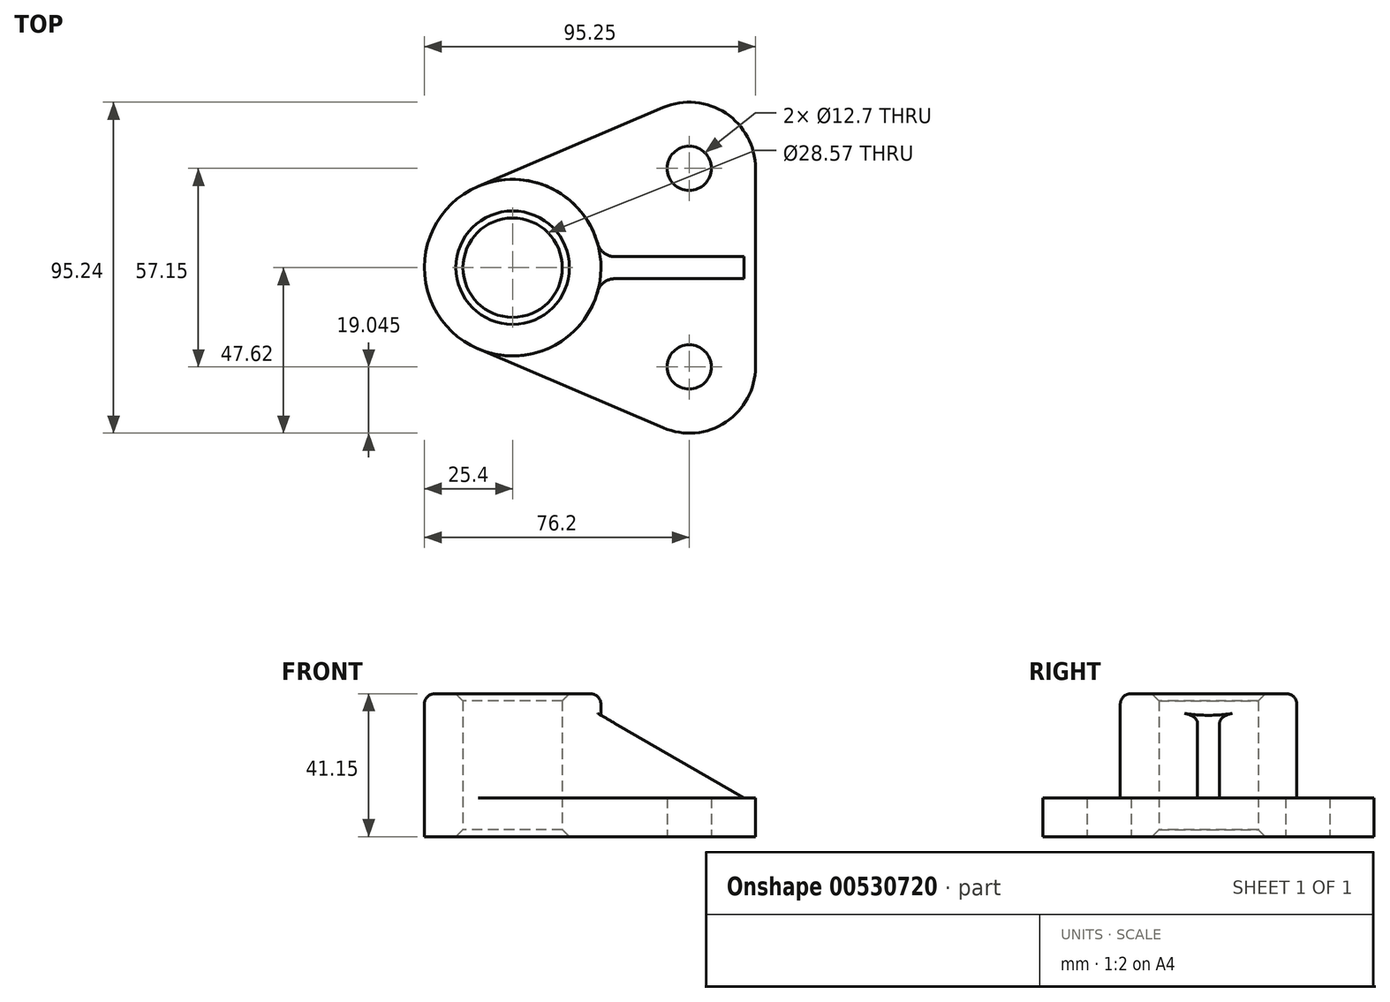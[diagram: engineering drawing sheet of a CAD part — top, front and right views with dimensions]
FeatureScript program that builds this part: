
annotation { "Feature Type Name" : "Feature", "Feature Type Description" : "" }
export const myFeature = defineFeature(function(context is Context, id is Id, definition is map)
    precondition{}
    {
        {
            var Q0;
            Q0=qCreatedBy(makeId("Top.planeOp"),FACE);
            var sketch = newSketch(context, id + "F0", { "sketchPlane" : qUnion([Q0])});
            skArc(sketch, "E0", {"start": v(25.4, 0) * mm, "mid": v(0, 25.4) * mm, "end": v(-25.4, 0) * mm});
            skArc(sketch, "E1", {"start": v(14.29, 0) * mm, "mid": v(0, 14.29) * mm, "end": v(-14.29, 0) * mm});
            skCircle(sketch, "E2", {"center": v(50.8, 28.57) * mm, "radius": 6.35 * mm});
            skArc(sketch, "E3", {"start": v(69.85, 28.57) * mm, "mid": v(61.3, 44.47) * mm, "end": v(43.33, 46.1) * mm});
            skLineSegment(sketch, "E4", {"start": v(-9.97, 23.36) * mm, "end": v(43.33, 46.1) * mm});
            skLineSegment(sketch, "E5", {"start": v(69.85, 28.57) * mm, "end": v(69.85, 0) * mm});
            skLineSegment(sketch, "E6", {"start": v(-25.4, 0) * mm, "end": v(69.85, 0) * mm, "construction": true});
            skLineSegment(sketch, "E7.MirrorCS", {"start": v(69.85, -28.58) * mm, "end": v(69.85, 0) * mm});
            skArc(sketch, "E8.MirrorCS", {"start": v(69.85, -28.58) * mm, "mid": v(61.3, -44.47) * mm, "end": v(43.33, -46.1) * mm});
            skCircle(sketch, "E9.MirrorC", {"center": v(50.8, -28.58) * mm, "radius": 6.35 * mm});
            skLineSegment(sketch, "E10.MirrorCS", {"start": v(-9.97, -23.36) * mm, "end": v(43.33, -46.1) * mm});
            skArc(sketch, "E11.MirrorCS", {"start": v(25.4, 0) * mm, "mid": v(0, -25.4) * mm, "end": v(-25.4, 0) * mm});
            skArc(sketch, "E12.MirrorCS", {"start": v(14.29, 0) * mm, "mid": v(0, -14.29) * mm, "end": v(-14.29, 0) * mm});
            skSolve(sketch);
        }
        {
            var Q0;
            Q0=makeQuery(id+"F0.imprint","IMPRINT",FACE,{"disambiguationData":[TD([[makeQuery(id+"F0.imprint","IMPRINT",EDGE,{"derivedFrom":sQuery(id+"F0.wireOp",EDGE,"E2")}),-1.0]])]});
            extrude(context, id + "F1", {"entities" : qUnion([Q0]), "depth" : 11.18 * mm});
        }
        {
            var Q0;
            Q0=makeQuery(id+"F0.imprint","IMPRINT",FACE,{"disambiguationData":[TD([[makeQuery(id+"F0.imprint","IMPRINT",EDGE,{"derivedFrom":sQuery(id+"F0.wireOp",EDGE,"E1")}),-1.0]])]});
            extrude(context, id + "F2", {"entities" : qUnion([Q0]), "operationType" : NewBodyOperationType.ADD, "depth" : 41.15 * mm});
        }
        {
            var Q0;
            Q0=qCreatedBy(makeId("Front.planeOp"),FACE);
            var sketch = newSketch(context, id + "F3", { "sketchPlane" : qUnion([Q0])});
            skLineSegment(sketch, "E13.0", {"start": v(69.85, 11.18) * mm, "end": v(43.33, 11.18) * mm});
            skLineSegment(sketch, "E14", {"start": v(69.85, 11.18) * mm, "end": v(66.55, 11.18) * mm});
            skLineSegment(sketch, "E15", {"start": v(66.55, 11.18) * mm, "end": v(22.55, 36.58) * mm});
            skLineSegment(sketch, "E16", {"start": v(43.33, 11.18) * mm, "end": v(22.55, 11.18) * mm});
            skLineSegment(sketch, "E17", {"start": v(22.55, 36.58) * mm, "end": v(22.55, 11.18) * mm});
            skSolve(sketch);
        }
        {
            var Q0;
            Q0=qSketchRegion(id+"F3",true);
            extrude(context, id + "F4", {"entities" : qUnion([Q0]), "operationType" : NewBodyOperationType.ADD, "endBound" : BoundingType.SYMMETRIC, "depth" : 6.35 * mm});
        }
        {
            var Q0;
            Q0=makeQuery(id+"F2.opExtrude","CAP_EDGE",EDGE,{"disambiguationData":[OSD([sQuery(id+"F0.wireOp",EDGE,"E0"),sQuery(id+"F0.wireOp",EDGE,"E11.MirrorCS")])],"isStart":false});
            fillet(context, id + "F5", {"entities" : qUnion([Q0]), "radius" : 3.05 * mm, "tangentPropagation" : true, "allowEdgeOverflow" : false});
        }
        {
            var Q0;
            {var subQ0=sQuery(id+"F0.wireOp",EDGE,"E11.MirrorCS");var subQ1=sQuery(id+"F0.wireOp",EDGE,"E10.MirrorCS");var subQ2=sQuery(id+"F0.wireOp",EDGE,"E0");Q0=makeQuery(id+"F4.boolean.opBoolean","SPLIT",EDGE,{"disambiguationData":[TD([makeQuery(id+"F1.opExtrude","SWEPT_FACE",FACE,{"disambiguationData":[OSD([subQ1])]})])],"derivedFrom":makeQuery(id+"F1.opExtrude","CAP_EDGE",EDGE,{"disambiguationData":[OSD([subQ2,subQ0])],"isStart":false})});}
            var Q1;
            {var subQ0=sQuery(id+"F0.wireOp",EDGE,"E11.MirrorCS");var subQ1=sQuery(id+"F0.wireOp",EDGE,"E4");var subQ2=sQuery(id+"F0.wireOp",EDGE,"E0");Q1=makeQuery(id+"F4.boolean.opBoolean","SPLIT",EDGE,{"disambiguationData":[TD([makeQuery(id+"F1.opExtrude","SWEPT_FACE",FACE,{"disambiguationData":[OSD([subQ1])]})])],"derivedFrom":makeQuery(id+"F1.opExtrude","CAP_EDGE",EDGE,{"disambiguationData":[OSD([subQ2,subQ0])],"isStart":false})});}
            var Q2;
            Q2=makeQuery(id+"F4.opExtrude","CAP_EDGE",EDGE,{"disambiguationData":[OSD([sQuery(id+"F3.wireOp",EDGE,"E13.0"),sQuery(id+"F3.wireOp",EDGE,"E16")])],"isStart":false});
            var Q3;
            Q3=makeQuery(id+"F4.boolean.opBoolean","INTERSECT",EDGE,{"derivedFrom":[makeQuery(id+"F2.opExtrude","SWEPT_FACE",FACE,{"disambiguationData":[OSD([sQuery(id+"F0.wireOp",EDGE,"E0"),sQuery(id+"F0.wireOp",EDGE,"E11.MirrorCS")])]}),makeQuery(id+"F4.opExtrude","CAP_FACE",FACE,{"disambiguationData":[OSD([sQuery(id+"F3.wireOp",EDGE,"E13.0"),sQuery(id+"F3.wireOp",EDGE,"E15"),sQuery(id+"F3.wireOp",EDGE,"E16"),sQuery(id+"F3.wireOp",EDGE,"E17")])],"isStart":false})]});
            var Q4;
            Q4=makeQuery(id+"F4.boolean.opBoolean","INTERSECT",EDGE,{"derivedFrom":[makeQuery(id+"F2.opExtrude","SWEPT_FACE",FACE,{"disambiguationData":[OSD([sQuery(id+"F0.wireOp",EDGE,"E0"),sQuery(id+"F0.wireOp",EDGE,"E11.MirrorCS")])]}),makeQuery(id+"F4.opExtrude","CAP_FACE",FACE,{"disambiguationData":[OSD([sQuery(id+"F3.wireOp",EDGE,"E13.0"),sQuery(id+"F3.wireOp",EDGE,"E15"),sQuery(id+"F3.wireOp",EDGE,"E16"),sQuery(id+"F3.wireOp",EDGE,"E17")])],"isStart":true})]});
            var Q5;
            Q5=makeQuery(id+"F4.opExtrude","CAP_EDGE",EDGE,{"disambiguationData":[OSD([sQuery(id+"F3.wireOp",EDGE,"E13.0"),sQuery(id+"F3.wireOp",EDGE,"E16")])],"isStart":true});
            fillet(context, id + "F6", {"entities" : qUnion([Q0, Q1, Q2, Q3, Q4, Q5]), "radius" : 5.08 * mm, "tangentPropagation" : true, "allowEdgeOverflow" : false});
        }
        {
            var Q0;
            Q0=makeQuery(id+"F2.opExtrude","CAP_EDGE",EDGE,{"disambiguationData":[OSD([sQuery(id+"F0.wireOp",EDGE,"E1"),sQuery(id+"F0.wireOp",EDGE,"E12.MirrorCS")])],"isStart":false});
            var Q1;
            Q1=makeQuery(id+"F2.opExtrude","CAP_EDGE",EDGE,{"disambiguationData":[OSD([sQuery(id+"F0.wireOp",EDGE,"E1"),sQuery(id+"F0.wireOp",EDGE,"E12.MirrorCS")])],"isStart":true});
            chamfer(context, id + "F7", {"entities" : qUnion([Q0, Q1]), "chamferType" : ChamferType.OFFSET_ANGLE, "width" : 2.03 * mm, "oppositeDirection" : false, "angle" : 45 * degree, "tangentPropagation" : true});
        }
    });
